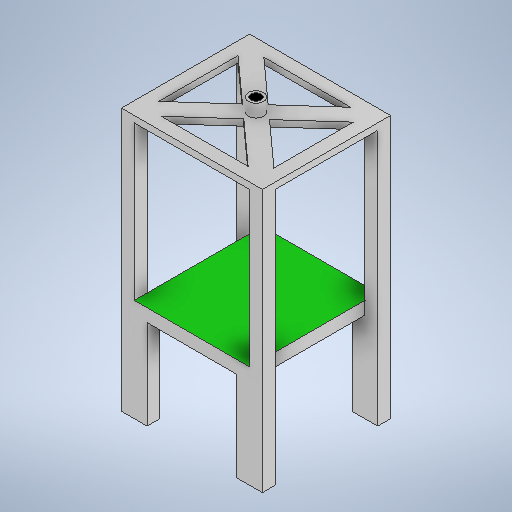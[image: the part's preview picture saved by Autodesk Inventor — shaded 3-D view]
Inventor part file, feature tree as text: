
AUTODESK INVENTOR PART (.ipt)
format: ipt  version: 2025.2 (Build 292293000, 293)  size: 384,512 bytes
history: native  units: mm
features: extrude x7, sketch x7, projected_geometry x4
ambient origin geometry x8: Origin, YZ Plane, XZ Plane, XY Plane, X Axis, Y Axis, Z Axis, Center Point
bodies: Solid1 (feature_tree)
feature tree (18):
  extrude  "Extrusion1"  Depth=1000.0mm
  extrude  "Extrusion2"  Depth=100.0mm
  extrude  "Extrusion3"  Depth=700.0mm
  extrude  "Extrusion4"  Depth=100.0mm
  extrude  "Extrusion5"  TaperAngle=0.0deg  [1 undecoded]
  extrude  "Extrusion6"  Depth=100.0mm
  extrude  "Extrusion7"  Depth=50.0mm TaperAngle=0.0deg
  sketch  "Sketch2"  dims[d0=900.0mm d1=1000.0mm]
  sketch  "Sketch3"  dims[d2=800.0mm d3=0.0mm d4=100.0mm]
  sketch  "Sketch4"  dims[d5=100.0mm d6=700.0mm]
  sketch  "Sketch5"  dims[d7=0.0mm d8=0.0mm d9=100.0mm]
  projected_geometry  "Projected Loop1"
  projected_geometry  "Projected Loop2"
  projected_geometry  "Projected Loop3"
  projected_geometry  "Projected Loop4"
  sketch  "Sketch6"  dims[d10=100.0mm d11=0.0mm d12=0.0mm]
  sketch  "Sketch7"  dims[d13=100.0mm d14=100.0mm]
  sketch  "Sketch8"  dims[d15=2000.0mm d16=0.0mm d17=50.0mm d18=0.0mm d19=100.0mm d20=80.0mm d21=200.0mm d22=0.0mm d23=120.0mm d24=100.0mm d25=0.0mm]
note: 1 required parameter value undecoded (feature->parameter linkage not recoverable at this tier; creation-order binding heuristic only, values carry confidence <= 0.55)
